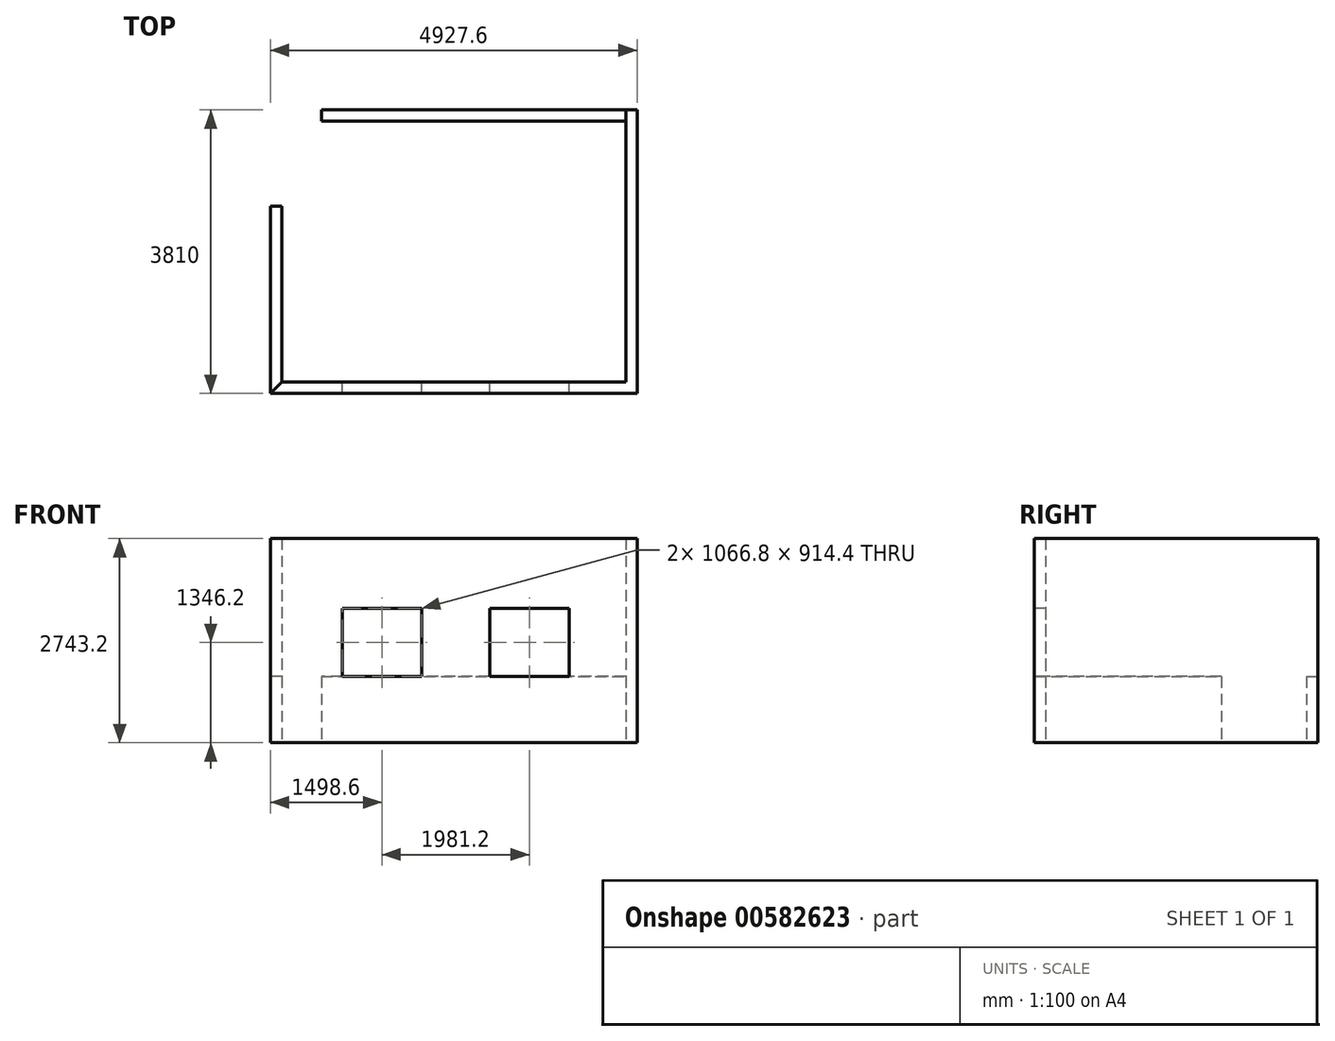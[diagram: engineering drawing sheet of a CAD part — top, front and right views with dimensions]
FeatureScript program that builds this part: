
annotation { "Feature Type Name" : "Feature", "Feature Type Description" : "" }
export const myFeature = defineFeature(function(context is Context, id is Id, definition is map)
    precondition{}
    {
        {
            var Q0;
            Q0=qCreatedBy(makeId("Top.planeOp"),FACE);
            var sketch = newSketch(context, id + "F0", { "sketchPlane" : qUnion([Q0])});
            skLineSegment(sketch, "E0.bottom", {"start": v(2311.4, 1752.6) * mm, "end": v(-2311.4, 1752.6) * mm});
            skLineSegment(sketch, "E0.top", {"start": v(2311.4, -1752.6) * mm, "end": v(-2311.4, -1752.6) * mm});
            skLineSegment(sketch, "E0.left", {"start": v(2311.4, 1752.6) * mm, "end": v(2311.4, -1752.6) * mm});
            skLineSegment(sketch, "E0.right", {"start": v(-2311.4, 1752.6) * mm, "end": v(-2311.4, -1752.6) * mm});
            skPoint(sketch, "E0.middle", {"position": v(0, 0) * mm});
            skLineSegment(sketch, "E1", {"start": v(-2311.4, -1752.6) * mm, "end": v(-2311.4, 609.6) * mm});
            skLineSegment(sketch, "E2", {"start": v(2311.4, 1752.6) * mm, "end": v(-1778, 1752.6) * mm});
            skLineSegment(sketch, "E3", {"start": v(-1778, 1752.6) * mm, "end": v(-2311.4, 609.6) * mm});
            skLineSegment(sketch, "E4.0", {"start": v(2463.8, -1905) * mm, "end": v(-2311.4, -1905) * mm});
            skLineSegment(sketch, "E4.1", {"start": v(2463.8, 1752.6) * mm, "end": v(2463.8, -1905) * mm});
            skLineSegment(sketch, "E5.0", {"start": v(2311.4, 1905) * mm, "end": v(-1778, 1905) * mm});
            skLineSegment(sketch, "E6.0", {"start": v(2311.4, -1905) * mm, "end": v(-2311.4, -1905) * mm});
            skLineSegment(sketch, "E7.0", {"start": v(-2463.8, -1752.6) * mm, "end": v(-2463.8, 609.6) * mm});
            skLineSegment(sketch, "E8", {"start": v(-2311.4, -1905) * mm, "end": v(-2463.8, -1905) * mm});
            skLineSegment(sketch, "E9", {"start": v(-2463.8, -1905) * mm, "end": v(-2463.8, -1752.6) * mm});
            skLineSegment(sketch, "E10", {"start": v(-2463.8, 609.6) * mm, "end": v(-2311.4, 609.6) * mm});
            skLineSegment(sketch, "E11", {"start": v(-1778, 1905) * mm, "end": v(-1778, 1752.6) * mm});
            skLineSegment(sketch, "E12", {"start": v(2311.4, 1905) * mm, "end": v(2463.8, 1905) * mm});
            skLineSegment(sketch, "E13", {"start": v(2463.8, 1905) * mm, "end": v(2463.8, 1752.6) * mm});
            skSolve(sketch);
        }
        {
            var Q0;
            Q0=makeQuery(id+"F0.imprint","IMPRINT",FACE,{"disambiguationData":[TD([[makeQuery(id+"F0.imprint","IMPRINT",EDGE,{"derivedFrom":sQuery(id+"F0.wireOp",EDGE,"E0.top")}),1.0]])]});
            extrude(context, id + "F1", {"entities" : qUnion([Q0]), "depth" : 889 * mm, "offsetDistance" : 25.4 * mm});
        }
        {
            var Q0;
            Q0=makeQuery(id+"F1.opExtrude","CAP_FACE",FACE,{"disambiguationData":[OSD([sQuery(id+"F0.wireOp",EDGE,"E0.top"),sQuery(id+"F0.wireOp",EDGE,"E0.left"),sQuery(id+"F0.wireOp",EDGE,"E1"),sQuery(id+"F0.wireOp",EDGE,"E2"),sQuery(id+"F0.wireOp",EDGE,"E4.0"),sQuery(id+"F0.wireOp",EDGE,"E4.1"),sQuery(id+"F0.wireOp",EDGE,"E5.0"),sQuery(id+"F0.wireOp",EDGE,"E6.0"),sQuery(id+"F0.wireOp",EDGE,"E7.0"),sQuery(id+"F0.wireOp",EDGE,"E8"),sQuery(id+"F0.wireOp",EDGE,"E9"),sQuery(id+"F0.wireOp",EDGE,"E10"),sQuery(id+"F0.wireOp",EDGE,"E11"),sQuery(id+"F0.wireOp",EDGE,"E12"),sQuery(id+"F0.wireOp",EDGE,"E13")])],"isStart":false});
            var sketch = newSketch(context, id + "F2", { "sketchPlane" : qUnion([Q0])});
            skLineSegment(sketch, "E14", {"start": v(2311.4, 1752.6) * mm, "end": v(2311.4, 1905) * mm});
            skLineSegment(sketch, "E15", {"start": v(2311.4, -1752.6) * mm, "end": v(2311.4, -1905) * mm});
            skSolve(sketch);
        }
        {
            var Q0;
            {var subQ2=sQuery(id+"F2.wireOp",EDGE,"E14");Q0=makeQuery(id+"F2.imprint","IMPRINT",FACE,{"disambiguationData":[TD([[makeQuery(id+"F2.imprint","IMPRINT",EDGE,{"derivedFrom":subQ2}),-1.0]])]});}
            extrude(context, id + "F3", {"entities" : qUnion([Q0]), "operationType" : NewBodyOperationType.ADD, "depth" : 2159 * mm, "offsetDistance" : 25.4 * mm});
        }
        {
            var Q0;
            {var subQ0=sQuery(id+"F0.wireOp",EDGE,"E8");var subQ1=sQuery(id+"F0.wireOp",EDGE,"E6.0");var subQ2=sQuery(id+"F0.wireOp",EDGE,"E4.0");var subQ3=sQuery(id+"F0.wireOp",EDGE,"E1");var subQ4=sQuery(id+"F0.wireOp",EDGE,"E0.left");var subQ5=sQuery(id+"F0.wireOp",EDGE,"E0.top");var subQ6=sQuery(id+"F0.wireOp",EDGE,"E9");var subQ7=sQuery(id+"F0.wireOp",EDGE,"E7.0");var subQ8=sQuery(id+"F0.wireOp",EDGE,"E10");Q0=makeQuery(id+"F3.boolean.opBoolean","SPLIT",FACE,{"disambiguationData":[TD([makeQuery(id+"F1.opExtrude","SWEPT_FACE",FACE,{"disambiguationData":[OSD([subQ5])]})])],"derivedFrom":makeQuery(id+"F1.opExtrude","CAP_FACE",FACE,{"disambiguationData":[OSD([subQ5,subQ4,subQ3,sQuery(id+"F0.wireOp",EDGE,"E2"),subQ2,sQuery(id+"F0.wireOp",EDGE,"E4.1"),sQuery(id+"F0.wireOp",EDGE,"E5.0"),subQ1,subQ7,subQ0,subQ6,subQ8,sQuery(id+"F0.wireOp",EDGE,"E11"),sQuery(id+"F0.wireOp",EDGE,"E12"),sQuery(id+"F0.wireOp",EDGE,"E13")])],"isStart":false})});}
            var sketch = newSketch(context, id + "F4", { "sketchPlane" : qUnion([Q0])});
            skLineSegment(sketch, "E16.bottom", {"start": v(2311.4, -1905) * mm, "end": v(1549.4, -1905) * mm});
            skLineSegment(sketch, "E16.top", {"start": v(2311.4, -1752.6) * mm, "end": v(1549.4, -1752.6) * mm});
            skLineSegment(sketch, "E16.left", {"start": v(2311.4, -1905) * mm, "end": v(2311.4, -1752.6) * mm});
            skLineSegment(sketch, "E16.right", {"start": v(1549.4, -1905) * mm, "end": v(1549.4, -1752.6) * mm});
            skLineSegment(sketch, "E17.bottom", {"start": v(2311.4, -1905) * mm, "end": v(482.6, -1905) * mm});
            skLineSegment(sketch, "E17.top", {"start": v(2311.4, -1752.6) * mm, "end": v(482.6, -1752.6) * mm});
            skLineSegment(sketch, "E17.right", {"start": v(482.6, -1905) * mm, "end": v(482.6, -1752.6) * mm});
            skLineSegment(sketch, "E18.bottom", {"start": v(2311.4, -1905) * mm, "end": v(-431.8, -1905) * mm});
            skLineSegment(sketch, "E18.top", {"start": v(2311.4, -1752.6) * mm, "end": v(-431.8, -1752.6) * mm});
            skLineSegment(sketch, "E18.right", {"start": v(-431.8, -1905) * mm, "end": v(-431.8, -1752.6) * mm});
            skLineSegment(sketch, "E19.bottom", {"start": v(2311.4, -1905) * mm, "end": v(-1498.6, -1905) * mm});
            skLineSegment(sketch, "E19.top", {"start": v(2311.4, -1752.6) * mm, "end": v(-1498.6, -1752.6) * mm});
            skLineSegment(sketch, "E19.right", {"start": v(-1498.6, -1905) * mm, "end": v(-1498.6, -1752.6) * mm});
            skLineSegment(sketch, "E20", {"start": v(-2311.4, -1752.6) * mm, "end": v(-2463.8, -1905) * mm});
            skSolve(sketch);
        }
        {
            var Q0;
            {var subQ0=sQuery(id+"F4.wireOp",EDGE,"E16.right");Q0=makeQuery(id+"F4.imprint","IMPRINT",FACE,{"disambiguationData":[TD([[makeQuery(id+"F4.imprint","IMPRINT",EDGE,{"derivedFrom":subQ0}),-1.0]])]});}
            var Q1;
            {var subQ0=sQuery(id+"F4.wireOp",EDGE,"E17.right");Q1=makeQuery(id+"F4.imprint","IMPRINT",FACE,{"disambiguationData":[TD([[makeQuery(id+"F4.imprint","IMPRINT",EDGE,{"derivedFrom":subQ0}),1.0]])]});}
            var Q2;
            {var subQ0=sQuery(id+"F4.wireOp",EDGE,"E19.right");Q2=makeQuery(id+"F4.imprint","IMPRINT",FACE,{"disambiguationData":[TD([[makeQuery(id+"F4.imprint","IMPRINT",EDGE,{"derivedFrom":subQ0}),1.0]])]});}
            extrude(context, id + "F5", {"entities" : qUnion([Q0, Q1, Q2]), "operationType" : NewBodyOperationType.ADD, "depth" : 2159 * mm, "offsetDistance" : 25.4 * mm});
        }
        {
            var Q0;
            Q0=makeQuery(id+"F5.opExtrude","SWEPT_FACE",FACE,{"disambiguationData":[OSD([sQuery(id+"F4.wireOp",EDGE,"E16.right")])]});
            var sketch = newSketch(context, id + "F6", { "sketchPlane" : qUnion([Q0])});
            skLineSegment(sketch, "E21", {"start": v(1752.6, 889) * mm, "end": v(1752.6, 1803.4) * mm});
            skLineSegment(sketch, "E22", {"start": v(1752.6, 1803.4) * mm, "end": v(1905, 1803.4) * mm});
            skSolve(sketch);
        }
        {
            var Q0;
            {var subQ0=sQuery(id+"F6.wireOp",EDGE,"E22");Q0=makeQuery(id+"F6.imprint","IMPRINT",FACE,{"disambiguationData":[TD([[makeQuery(id+"F6.imprint","IMPRINT",EDGE,{"derivedFrom":subQ0}),1.0]])]});}
            extrude(context, id + "F7", {"entities" : qUnion([Q0]), "operationType" : NewBodyOperationType.ADD, "endBound" : BoundingType.UP_TO_NEXT, "depth" : 25.4 * mm, "offsetDistance" : 25.4 * mm});
        }
        {
            var Q0;
            Q0=makeQuery(id+"F5.opExtrude","SWEPT_FACE",FACE,{"disambiguationData":[OSD([sQuery(id+"F4.wireOp",EDGE,"E18.right")])]});
            var sketch = newSketch(context, id + "F8", { "sketchPlane" : qUnion([Q0])});
            skLineSegment(sketch, "E23", {"start": v(1752.6, 889) * mm, "end": v(1752.6, 1803.4) * mm});
            skLineSegment(sketch, "E24", {"start": v(1752.6, 1803.4) * mm, "end": v(1905, 1803.4) * mm});
            skSolve(sketch);
        }
        {
            var Q0;
            {var subQ0=sQuery(id+"F8.wireOp",EDGE,"E24");Q0=makeQuery(id+"F8.imprint","IMPRINT",FACE,{"disambiguationData":[TD([[makeQuery(id+"F8.imprint","IMPRINT",EDGE,{"derivedFrom":subQ0}),1.0]])]});}
            extrude(context, id + "F9", {"entities" : qUnion([Q0]), "operationType" : NewBodyOperationType.ADD, "endBound" : BoundingType.UP_TO_NEXT, "depth" : 25.4 * mm, "offsetDistance" : 25.4 * mm});
        }
        {
            var Q0;
            {var subQ0=sQuery(id+"F4.wireOp",EDGE,"E18.right");var subQ1=sQuery(id+"F4.wireOp",EDGE,"E16.right");var subQ2=sQuery(id+"F4.wireOp",EDGE,"E19.top");var subQ3=sQuery(id+"F4.wireOp",EDGE,"E19.bottom");var subQ4=sQuery(id+"F0.wireOp",EDGE,"E8");var subQ5=sQuery(id+"F0.wireOp",EDGE,"E6.0");var subQ6=sQuery(id+"F0.wireOp",EDGE,"E4.0");Q0=makeQuery(id+"F9.boolean.opBoolean","MERGE",FACE,{"derivedFrom":[makeQuery(id+"F5.opExtrude","CAP_FACE",FACE,{"disambiguationData":[OSD([sQuery(id+"F0.wireOp",EDGE,"E0.top"),subQ6,subQ5,subQ4,sQuery(id+"F4.wireOp",EDGE,"E19.right"),sQuery(id+"F4.wireOp",EDGE,"E20")])],"isStart":false}),makeQuery(id+"F7.boolean.opBoolean","MERGE",FACE,{"derivedFrom":[makeQuery(id+"F5.opExtrude","CAP_FACE",FACE,{"disambiguationData":[OSD([sQuery(id+"F4.wireOp",EDGE,"E17.right"),subQ0,subQ3,subQ2])],"isStart":false}),makeQuery(id+"F5.boolean.opBoolean","MERGE",FACE,{"derivedFrom":[makeQuery(id+"F3.opExtrude","CAP_FACE",FACE,{"disambiguationData":[OSD([sQuery(id+"F0.wireOp",EDGE,"E0.left"),subQ6,sQuery(id+"F0.wireOp",EDGE,"E4.1"),sQuery(id+"F0.wireOp",EDGE,"E5.0"),subQ5,subQ4,sQuery(id+"F0.wireOp",EDGE,"E12"),sQuery(id+"F0.wireOp",EDGE,"E13"),sQuery(id+"F2.wireOp",EDGE,"E14"),sQuery(id+"F2.wireOp",EDGE,"E15")])],"isStart":false}),makeQuery(id+"F5.opExtrude","CAP_FACE",FACE,{"disambiguationData":[OSD([subQ1,subQ3,subQ2,sQuery(id+"F4.wireOp",EDGE,"E16.left")])],"isStart":false})]}),makeQuery(id+"F7.opExtrude","SWEPT_FACE",FACE,{"disambiguationData":[OSD([subQ1])]})]}),makeQuery(id+"F9.opExtrude","SWEPT_FACE",FACE,{"disambiguationData":[OSD([subQ0])]})]});}
            extrude(context, id + "F10", {"entities" : qUnion([Q0]), "operationType" : NewBodyOperationType.REMOVE, "oppositeDirection" : true, "depth" : 304.8 * mm, "offsetDistance" : 25.4 * mm});
        }
    });
